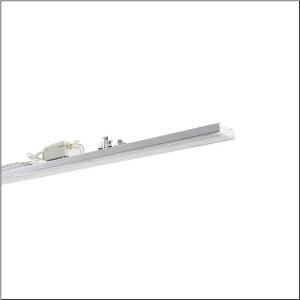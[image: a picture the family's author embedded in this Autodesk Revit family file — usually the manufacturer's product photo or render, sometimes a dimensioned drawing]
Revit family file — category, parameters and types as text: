
# Revit family: licross_r__21_recessed_ho_52te12cn4c5m_727f
name_source: partatom
category: Lighting Fixtures
units: mm (PartAtom-declared; Revit-internal decimal feet)

## family parameters
Cut with Voids When Loaded = No
Host = Face
Light Source = No
Part Type = Normal
Room Calculation Point = No
Round Connector Dimension = Use Diameter
Shared = No

## types (1)
- --- (1 x LED, 12670 lm, 68.4 W, 4000K)
    Apparent Load = 68 VA
    CIE Flux Codes = 69 91 98 100 100
    Color Rendering = 80
    Color Temperature = 4000K
    Default Elevation = 1800 mm
    Description = Licross® 21 Recessed HO, luminaire insert, of sheet steel, galvanised, coil coated, white, length: 1.500mm, width: 66mm, height: 67mm, LED rated luminous flux: 12.670lm, light colour: 840, control gear: ON/OFF Multilumen, CLOi, control gear: ECG Multilumen, with plug, 3-pole, with phase selection, mains connection: 220..240V, AC, 50/60Hz, start of lifetime: 68W, end of service life: 83W, halogen-free wiring, primary optical cover: cover, of PMMA, light emission: direct distribution, primary light characteristic: symmetric, protection rating (complete): IP54, insulation class (complete): insulation class I (protective earthing), certification: CE, ENEC, VDE, UKCA, protection symbol: D if used in an environment with non-conductive dust loads with corresponding accessories, impact resistance: IK06, permissible ambient temperature for indoor applications: -35..+30°C, corresponds to IFS (International Featured Standards) requirements for safety and quality in the food industry, reducing of maximum allowable ambient temperature of 5°C with ceiling mounting, LABS conformity tested according to VDMA 24364:2018-05, packaging unit: 1 piece
    Height = 58 mm
    Lamp = 1 x LED
    Lamp Light Flux = 12670 lm
    Lamp Power = 68.4 W
    Lamp count = 1
    Length = 1500 mm
    Luminous efficacy = 185 lm/W
    Manufacturer = Siteco
    ModVariant = No
    Model = 52TE12CN4C5M
    Mounting Place = Ceiling
    Mounting Type = Pendant
    Number of Poles = 1
    OnlyDefault = Yes
    Power Factor = 1
    Product Name = Licross® 21 Recessed HO
    Product group = luminaire insert
    ProductGroupID = 901
    Protection Class = Protection class I
    Protection Degree = IP 54
    RLX_Detail_Level = 1
    RLX_Emergency_Light_Flux = 0 lm
    RLX_Emergency_Type = 0
    RLX_Emergency_Type_DB = No
    RlxData = <blob elided: 22405 chars, md5=fb08d1a3>
    Socket = socket
    Standby Power = 0 W
    System Light Flux = 12670 lm
    System Power = 68 W
    Type Comments = factory setting: luminous flux: 100 % | (A | C | E) | 161 mA
    Type Image = l_1296930.jpg
    URL = http://relux.com
    VarID = @adj_039969
    Voltage = 0 V
    Weight = 0.00 kg
    Width = 66 mm

## geometry (parser evidence)
native form markers: Blend x4, Sweep x14
no freeform markers — native parametric forms only
